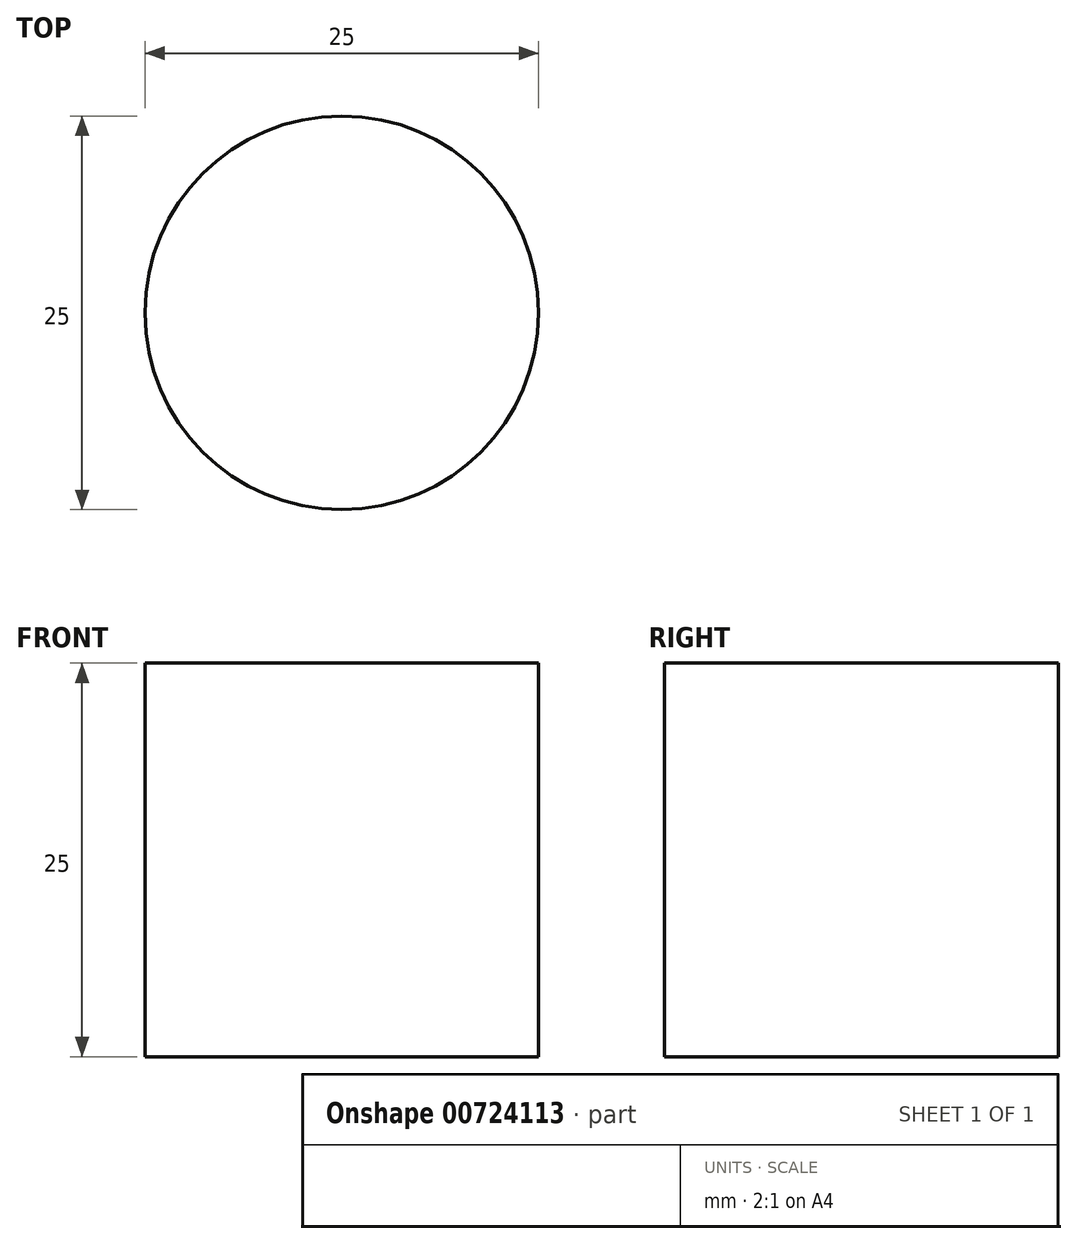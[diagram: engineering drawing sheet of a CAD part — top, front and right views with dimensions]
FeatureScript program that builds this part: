
annotation { "Feature Type Name" : "Feature", "Feature Type Description" : "" }
export const myFeature = defineFeature(function(context is Context, id is Id, definition is map)
    precondition{}
    {
        {
            var Q0;
            Q0=qCreatedBy(makeId("Top.planeOp"),FACE);
            var sketch = newSketch(context, id + "F0", { "sketchPlane" : qUnion([Q0])});
            skCircle(sketch, "E0", {"center": v(0, 0) * mm, "radius": 12.5 * mm});
            skSolve(sketch);
        }
        {
            var Q0;
            Q0 = qSketchRegion(id + "F0", true);
            extrude(context, id + "F1", {"entities" : qUnion([Q0]), "depth" : 25 * mm, "offsetDistance" : 25 * mm});
        }
    });
